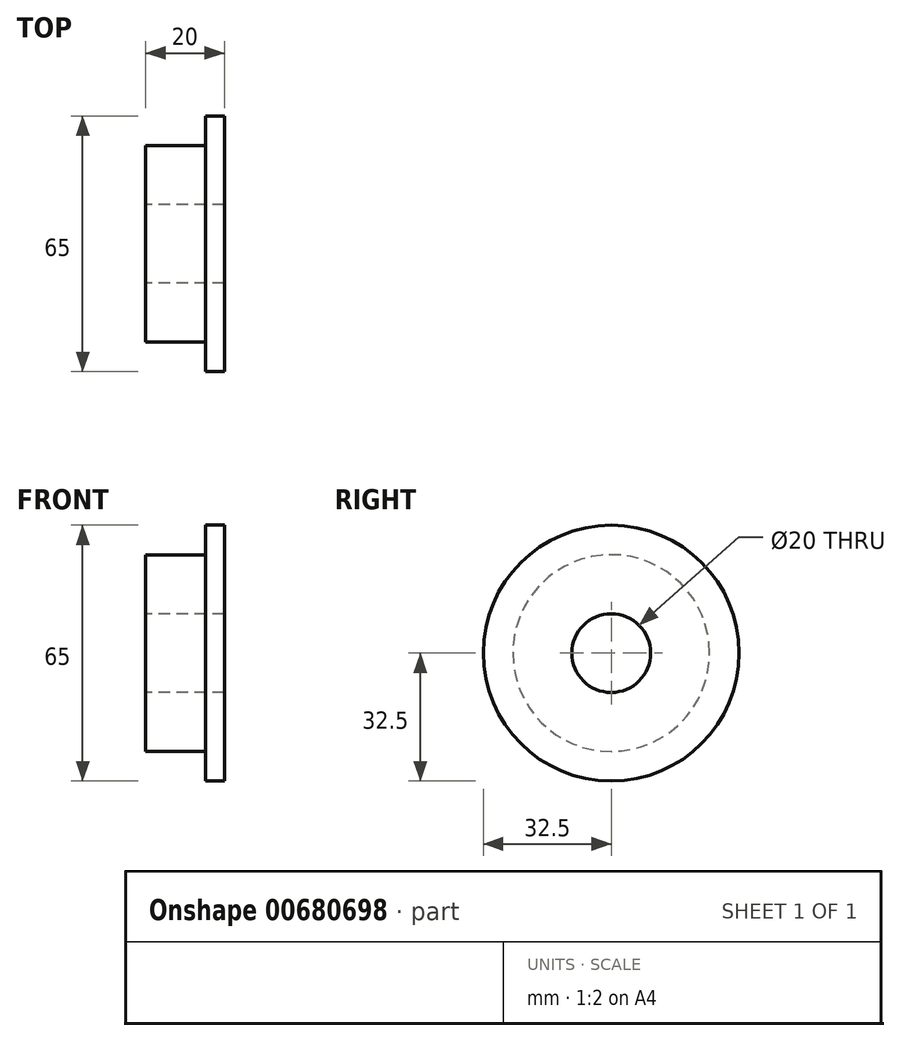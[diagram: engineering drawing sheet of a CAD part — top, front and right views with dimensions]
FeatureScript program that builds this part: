
annotation { "Feature Type Name" : "Feature", "Feature Type Description" : "" }
export const myFeature = defineFeature(function(context is Context, id is Id, definition is map)
    precondition{}
    {
        {
            var Q0;
            Q0=qCreatedBy(makeId("Right.planeOp"),FACE);
            var sketch = newSketch(context, id + "F0", { "sketchPlane" : qUnion([Q0])});
            skCircle(sketch, "E0", {"center": v(0, 0) * mm, "radius": 32.5 * mm});
            skCircle(sketch, "E1", {"center": v(0, 0) * mm, "radius": 10 * mm});
            skSolve(sketch);
        }
        {
            var Q0;
            Q0 = qSketchRegion(id + "F0", true);
            extrude(context, id + "F1", {"entities" : qUnion([Q0]), "depth" : 20 * mm, "offsetDistance" : 25 * mm});
        }
        {
            var Q0;
            Q0=makeQuery(id+"F1.opExtrude","CAP_FACE",FACE,{"disambiguationData":[OSD([sQuery(id+"F0.wireOp",EDGE,"E0"),sQuery(id+"F0.wireOp",EDGE,"E1")])],"isStart":true});
            var sketch = newSketch(context, id + "F2", { "sketchPlane" : qUnion([Q0])});
            skCircle(sketch, "E2", {"center": v(0, 0) * mm, "radius": 25 * mm});
            skCircle(sketch, "E3", {"center": v(0, 0) * mm, "radius": 43.12 * mm});
            skSolve(sketch);
        }
        {
            var Q0;
            Q0 = qSketchRegion(id + "F2", true);
            extrude(context, id + "F3", {"entities" : qUnion([Q0]), "operationType" : NewBodyOperationType.REMOVE, "oppositeDirection" : true, "depth" : 15.25 * mm, "offsetDistance" : 25 * mm});
        }
    });
